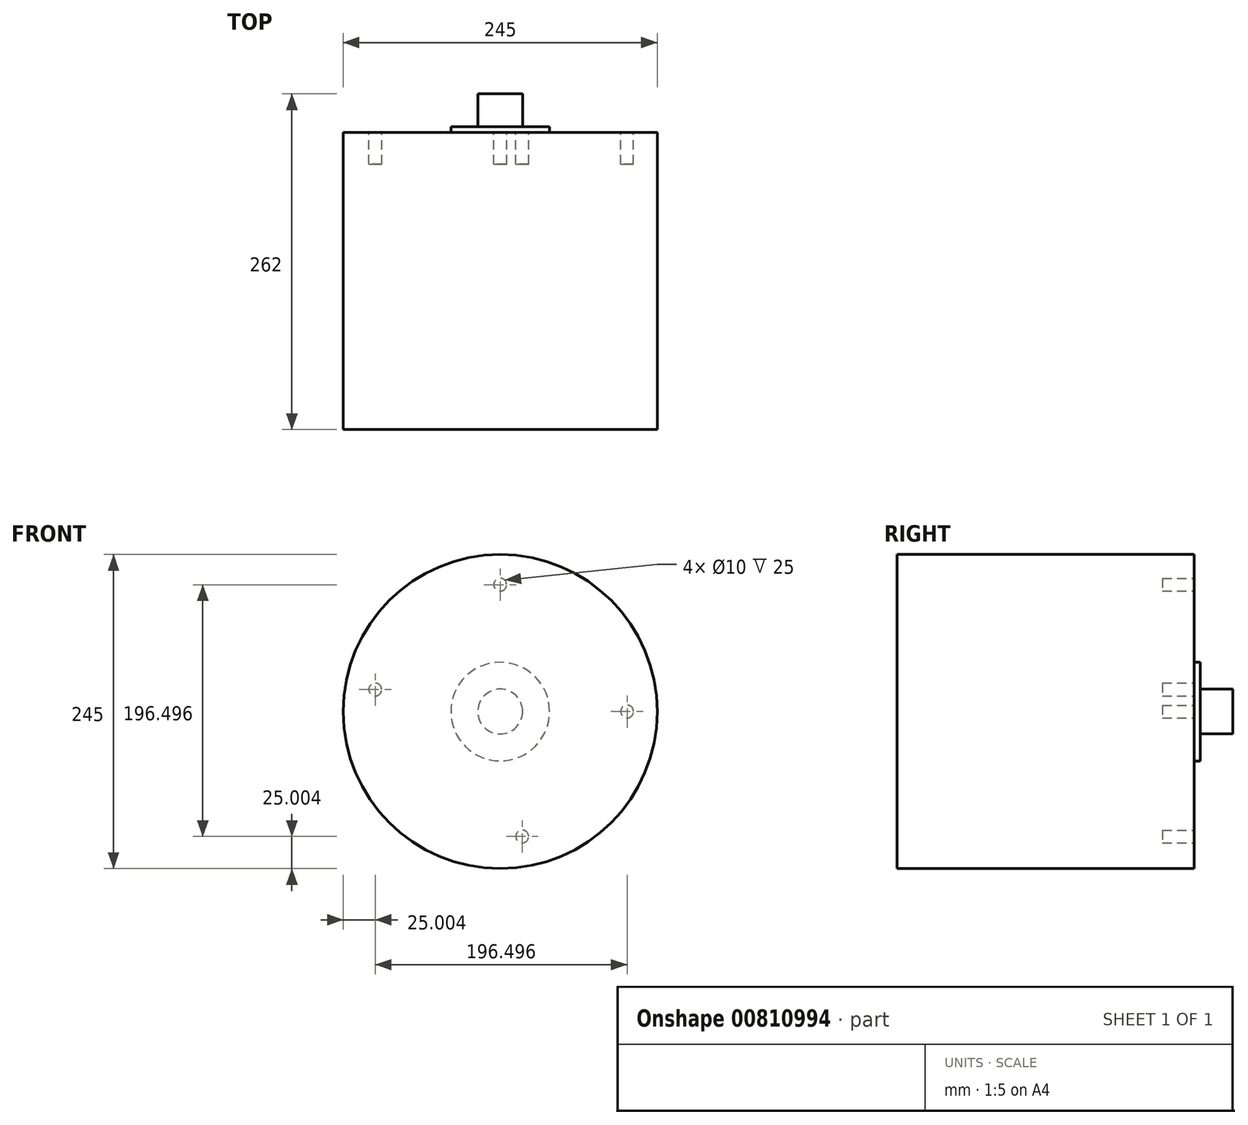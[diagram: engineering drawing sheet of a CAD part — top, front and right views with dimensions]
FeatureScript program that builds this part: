
annotation { "Feature Type Name" : "Feature", "Feature Type Description" : "" }
export const myFeature = defineFeature(function(context is Context, id is Id, definition is map)
    precondition{}
    {
        {
            var Q0;
            Q0=qCreatedBy(makeId("Front.planeOp"),FACE);
            var sketch = newSketch(context, id + "F0", { "sketchPlane" : qUnion([Q0])});
            skCircle(sketch, "E0", {"center": v(0, 0) * mm, "radius": 17.5 * mm});
            skSolve(sketch);
        }
        {
            var Q0;
            Q0=makeQuery(id+"F0.imprint","IMPRINT",FACE,{"disambiguationData":[TD([[makeQuery(id+"F0.imprint","IMPRINT",EDGE,{"derivedFrom":sQuery(id+"F0.wireOp",EDGE,"E0")}),1.0]])]});
            extrude(context, id + "F1", {"entities" : qUnion([Q0]), "oppositeDirection" : true, "depth" : 30 * mm, "offsetDistance" : 25 * mm});
        }
        {
            var Q0;
            Q0=qCreatedBy(makeId("Front.planeOp"),FACE);
            var sketch = newSketch(context, id + "F2", { "sketchPlane" : qUnion([Q0])});
            skCircle(sketch, "E1", {"center": v(0, 0) * mm, "radius": 38.5 * mm});
            skSolve(sketch);
        }
        {
            var Q0;
            Q0 = qSketchRegion(id + "F2", true);
            extrude(context, id + "F3", {"entities" : qUnion([Q0]), "operationType" : NewBodyOperationType.ADD, "oppositeDirection" : true, "depth" : 4.5 * mm, "offsetDistance" : 25 * mm});
        }
        {
            var Q0;
            Q0=qCreatedBy(makeId("Front.planeOp"),FACE);
            var sketch = newSketch(context, id + "F4", { "sketchPlane" : qUnion([Q0])});
            skCircle(sketch, "E2", {"center": v(0, 0) * mm, "radius": 122.5 * mm});
            skSolve(sketch);
        }
        {
            var Q0;
            Q0 = qSketchRegion(id + "F4", true);
            extrude(context, id + "F5", {"entities" : qUnion([Q0]), "operationType" : NewBodyOperationType.ADD, "depth" : 232 * mm, "offsetDistance" : 25 * mm});
        }
        {
            var Q0;
            Q0=makeQuery(id+"F5.opExtrude","CAP_FACE",FACE,{"disambiguationData":[OSD([sQuery(id+"F4.wireOp",EDGE,"E2")])],"isStart":true});
            var sketch = newSketch(context, id + "F6", { "sketchPlane" : qUnion([Q0])});
            skCircle(sketch, "E3", {"center": v(0, 0) * mm, "radius": 99 * mm, "construction": true});
            skCircle(sketch, "E4", {"center": v(-99, 0) * mm, "radius": 5 * mm});
            skCircle(sketch, "E5", {"center": v(0, 99) * mm, "radius": 5 * mm});
            skCircle(sketch, "E6", {"center": v(97.5, 17.2) * mm, "radius": 5 * mm});
            skCircle(sketch, "E7", {"center": v(-17.2, -97.5) * mm, "radius": 5 * mm});
            skLineSegment(sketch, "E8", {"start": v(0, 0) * mm, "end": v(-99, 0) * mm, "construction": true});
            skLineSegment(sketch, "E9", {"start": v(0, 0) * mm, "end": v(0, 99) * mm, "construction": true});
            skLineSegment(sketch, "E10", {"start": v(0, 0) * mm, "end": v(97.5, 17.2) * mm, "construction": true});
            skLineSegment(sketch, "E11", {"start": v(0, 0) * mm, "end": v(-17.2, -97.5) * mm, "construction": true});
            skSolve(sketch);
        }
        {
            var Q0;
            Q0 = qSketchRegion(id + "F6", true);
            extrude(context, id + "F7", {"entities" : qUnion([Q0]), "operationType" : NewBodyOperationType.REMOVE, "oppositeDirection" : true, "depth" : 25 * mm, "offsetDistance" : 25.4 * mm});
        }
    });
